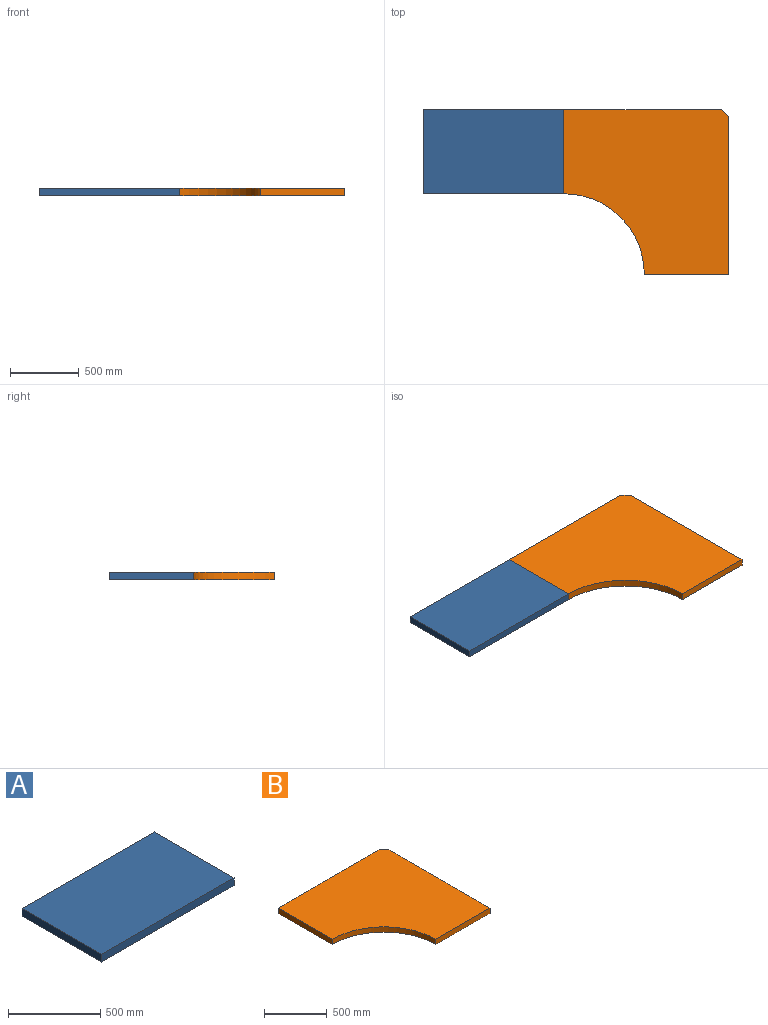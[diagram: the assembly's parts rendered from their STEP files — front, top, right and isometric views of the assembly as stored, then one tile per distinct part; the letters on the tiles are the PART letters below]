
ASSEMBLY  parts=2 mates=1
PART A: 6 faces, bbox 1016x609.6x50.8 mm
  f0: plane 609.6x50.8mm, normal (1,0,0), area 30967.7mm2, adj f1,f3,f4,f5
  f1: plane 1016x50.8mm, normal (0,1,0), area 51612.8mm2, adj f0,f2,f4,f5
  f2: plane 609.6x50.8mm, normal (-1,0,0), area 30967.7mm2, adj f1,f3,f4,f5
  f3: plane 1016x50.8mm, normal (0,-1,0), area 51612.8mm2, adj f0,f2,f4,f5
  f4: plane 1016x609.6mm, normal (0,0,1), area 619353.6mm2, adj f0,f1,f2,f3
  f5: plane 1016x609.6mm, normal (0,0,-1), area 619353.6mm2, adj f0,f1,f2,f3
PART B: 8 faces, bbox 1193.8x1193.8x50.8 mm
  f0: plane 1143x50.8mm, normal (0,1,0), area 58064.4mm2, adj f1,f5,f6,f7
  f1: plane 609.6x50.8mm, normal (-1,0,0), area 30967.7mm2, adj f0,f2,f6,f7
  f2: cylinder r=584.2mm len=584.2mm, axis (0,0,-1), area 46617.1mm2, adj f1,f3,f6,f7
  f3: plane 609.6x50.8mm, normal (0,-1,0), area 30967.7mm2, adj f2,f4,f6,f7
  f4: plane 1143x50.8mm, normal (1,0,0), area 58064.4mm2, adj f3,f5,f6,f7
  f5: plane 50.8x50.8mm, normal (0.71,0.71,0), area 3649.6mm2, adj f0,f4,f6,f7
  f6: plane 1193.8x1193.8mm, normal (0,0,1), area 1155819.9mm2, adj f0,f1,f2,f3,f4,f5
  f7: plane 1193.8x1193.8mm, normal (0,0,-1), area 1155819.9mm2, adj f0,f1,f2,f3,f4,f5
PLACE A t=(-596.9,-546.1,0)mm
PLACE B t=(-596.9,-546.1,0)mm
MATE fastened B.f1 <-> A.f0  axis (-1,0,0) through (-1193.8,-254,25.4)mm
